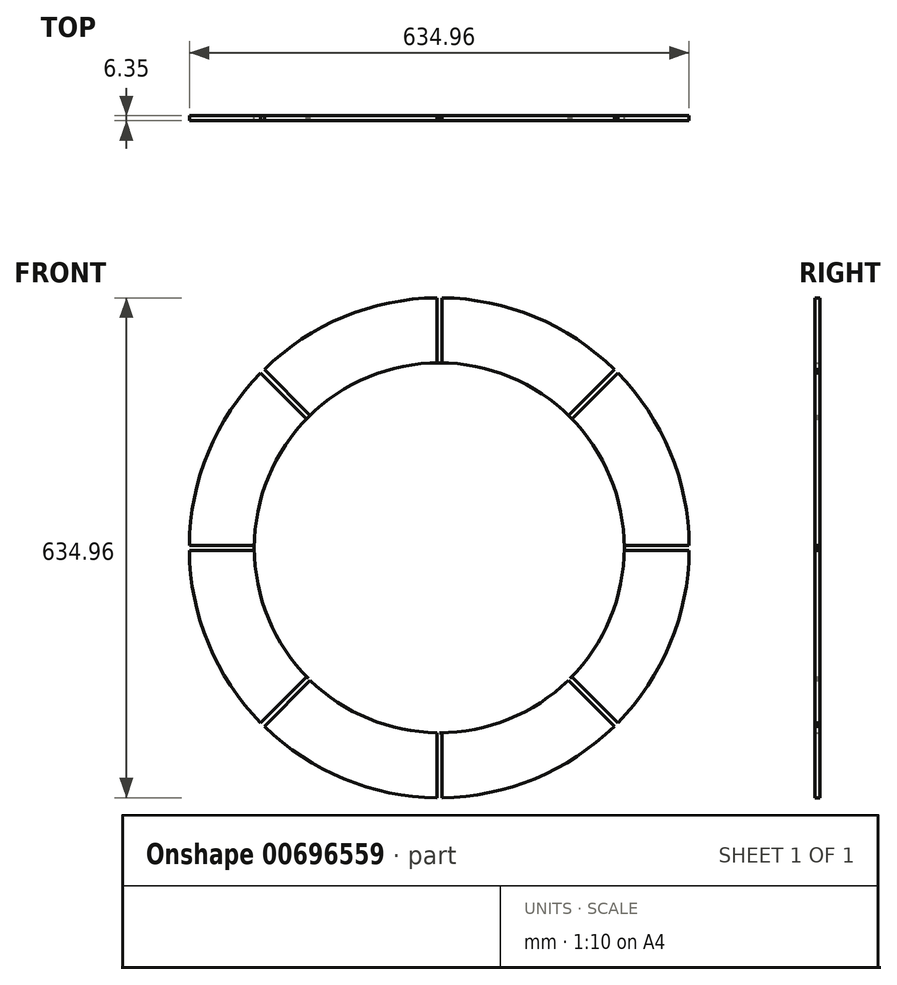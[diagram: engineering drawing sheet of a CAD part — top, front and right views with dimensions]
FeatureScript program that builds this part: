
annotation { "Feature Type Name" : "Feature", "Feature Type Description" : "" }
export const myFeature = defineFeature(function(context is Context, id is Id, definition is map)
    precondition{}
    {
        {
            var Q0;
            Q0=qCreatedBy(makeId("Front.planeOp"),FACE);
            var sketch = newSketch(context, id + "F0", { "sketchPlane" : qUnion([Q0])});
            skCircle(sketch, "E0", {"center": v(0, 0) * mm, "radius": 234.95 * mm});
            skCircle(sketch, "E1", {"center": v(0, 0) * mm, "radius": 317.5 * mm});
            skLineSegment(sketch, "E2", {"start": v(317.48, 0) * mm, "end": v(317.5, 0) * mm});
            skLineSegment(sketch, "E3", {"start": v(317.5, 0) * mm, "end": v(317.48, 0) * mm});
            skLineSegment(sketch, "E4", {"start": v(-317.48, 0) * mm, "end": v(-317.5, 0) * mm});
            skLineSegment(sketch, "E5", {"start": v(0, 317.5) * mm, "end": v(0, 317.5) * mm});
            skLineSegment(sketch, "E6", {"start": v(0, -317.48) * mm, "end": v(0, -317.5) * mm});
            skLineSegment(sketch, "E7.bottom", {"start": v(-317.5, 0) * mm, "end": v(-317.48, 0) * mm});
            skLineSegment(sketch, "E8", {"start": v(-224.5, 224.5) * mm, "end": v(-224.5, 224.5) * mm});
            skLineSegment(sketch, "E9", {"start": v(224.5, 224.5) * mm, "end": v(224.5, 224.5) * mm});
            skLineSegment(sketch, "E10", {"start": v(-224.5, -224.5) * mm, "end": v(-224.5, -224.5) * mm});
            skLineSegment(sketch, "E11", {"start": v(224.5, -224.5) * mm, "end": v(224.5, -224.5) * mm});
            skLineSegment(sketch, "E12", {"start": v(-166.13, -166.13) * mm, "end": v(-163.87, -168.36) * mm});
            skLineSegment(sketch, "E13", {"start": v(-166.13, -166.13) * mm, "end": v(-168.38, -163.89) * mm});
            skLineSegment(sketch, "E14", {"start": v(-168.38, -163.89) * mm, "end": v(-226.74, -222.25) * mm});
            skLineSegment(sketch, "E15", {"start": v(-163.87, -168.36) * mm, "end": v(-221.85, -227.13) * mm});
            skLineSegment(sketch, "E16", {"start": v(-221.85, -227.13) * mm, "end": v(-226.74, -222.25) * mm});
            skLineSegment(sketch, "E17", {"start": v(0, -234.95) * mm, "end": v(-3.17, -234.93) * mm});
            skLineSegment(sketch, "E18", {"start": v(0, -234.95) * mm, "end": v(3.18, -234.95) * mm});
            skLineSegment(sketch, "E19", {"start": v(-3.17, -234.93) * mm, "end": v(-3.17, -317.48) * mm});
            skLineSegment(sketch, "E20", {"start": v(3.18, -234.95) * mm, "end": v(3.18, -317.48) * mm});
            skLineSegment(sketch, "E21", {"start": v(3.18, -317.48) * mm, "end": v(-3.17, -317.48) * mm});
            skLineSegment(sketch, "E22", {"start": v(166.13, -166.13) * mm, "end": v(163.74, -168.22) * mm});
            skLineSegment(sketch, "E23", {"start": v(166.13, -166.13) * mm, "end": v(168.38, -163.89) * mm});
            skLineSegment(sketch, "E24", {"start": v(163.74, -168.22) * mm, "end": v(222.26, -226.73) * mm});
            skLineSegment(sketch, "E25", {"start": v(168.38, -163.89) * mm, "end": v(226.74, -222.25) * mm});
            skLineSegment(sketch, "E26", {"start": v(226.74, -222.25) * mm, "end": v(222.26, -226.73) * mm});
            skLineSegment(sketch, "E27", {"start": v(234.95, 0) * mm, "end": v(234.95, -3.17) * mm});
            skLineSegment(sketch, "E28", {"start": v(234.95, 0) * mm, "end": v(234.95, 3.18) * mm});
            skLineSegment(sketch, "E29", {"start": v(234.95, 3.18) * mm, "end": v(317.48, 3.18) * mm});
            skLineSegment(sketch, "E30", {"start": v(317.48, 3.18) * mm, "end": v(317.48, -3.18) * mm});
            skLineSegment(sketch, "E31", {"start": v(317.48, -3.18) * mm, "end": v(234.95, -3.17) * mm});
            skLineSegment(sketch, "E32", {"start": v(166.13, 166.13) * mm, "end": v(168.38, 163.89) * mm});
            skLineSegment(sketch, "E33", {"start": v(166.13, 166.13) * mm, "end": v(163.89, 168.38) * mm});
            skLineSegment(sketch, "E34", {"start": v(168.38, 163.89) * mm, "end": v(226.74, 222.25) * mm});
            skLineSegment(sketch, "E35", {"start": v(226.74, 222.25) * mm, "end": v(222.25, 226.74) * mm});
            skLineSegment(sketch, "E36", {"start": v(222.25, 226.74) * mm, "end": v(163.89, 168.38) * mm});
            skLineSegment(sketch, "E37", {"start": v(0, 234.95) * mm, "end": v(3.17, 234.95) * mm});
            skLineSegment(sketch, "E38", {"start": v(0, 234.95) * mm, "end": v(-3.17, 234.95) * mm});
            skLineSegment(sketch, "E39", {"start": v(-3.17, 234.95) * mm, "end": v(-3.17, 317.48) * mm});
            skLineSegment(sketch, "E40", {"start": v(-3.17, 317.48) * mm, "end": v(3.17, 317.5) * mm});
            skLineSegment(sketch, "E41", {"start": v(3.17, 317.5) * mm, "end": v(3.17, 234.95) * mm});
            skLineSegment(sketch, "E42", {"start": v(-166.13, 166.13) * mm, "end": v(-168.38, 163.89) * mm});
            skLineSegment(sketch, "E43", {"start": v(-166.13, 166.13) * mm, "end": v(-163.89, 168.38) * mm});
            skLineSegment(sketch, "E44", {"start": v(-168.38, 163.89) * mm, "end": v(-226.74, 222.25) * mm});
            skLineSegment(sketch, "E45", {"start": v(-226.74, 222.25) * mm, "end": v(-222.25, 226.74) * mm});
            skLineSegment(sketch, "E46", {"start": v(-222.25, 226.74) * mm, "end": v(-163.89, 168.38) * mm});
            skLineSegment(sketch, "E47", {"start": v(-234.95, 0) * mm, "end": v(-234.95, -3.18) * mm});
            skLineSegment(sketch, "E48", {"start": v(-234.95, 0) * mm, "end": v(-234.95, 3.17) * mm});
            skLineSegment(sketch, "E49", {"start": v(-234.95, 3.17) * mm, "end": v(-317.48, 3.17) * mm});
            skLineSegment(sketch, "E50", {"start": v(-317.48, 3.17) * mm, "end": v(-317.48, -3.18) * mm});
            skLineSegment(sketch, "E51", {"start": v(-317.48, -3.17) * mm, "end": v(-234.95, -3.18) * mm});
            skSolve(sketch);
        }
        {
            var Q0;
            Q0=makeQuery(id+"F0.imprint","IMPRINT",FACE,{"disambiguationData":[TD([[makeQuery(id+"F0.imprint","IMPRINT",EDGE,{"derivedFrom":sQuery(id+"F0.wireOp",EDGE,"E0")}),-1.0]])]});
            var Q1;
            {var subQ1=sQuery(id+"F0.wireOp",EDGE,"E13");Q1=makeQuery(id+"F0.imprint","IMPRINT",FACE,{"disambiguationData":[TD([[makeQuery(id+"F0.imprint","IMPRINT",EDGE,{"derivedFrom":subQ1}),-1.0]])]});}
            var Q2;
            {var subQ3=sQuery(id+"F0.wireOp",EDGE,"E42");Q2=makeQuery(id+"F0.imprint","IMPRINT",FACE,{"disambiguationData":[TD([[makeQuery(id+"F0.imprint","IMPRINT",EDGE,{"derivedFrom":subQ3}),1.0]])]});}
            var Q3;
            {var subQ0=sQuery(id+"F0.wireOp",EDGE,"E38");Q3=makeQuery(id+"F0.imprint","IMPRINT",FACE,{"disambiguationData":[TD([[makeQuery(id+"F0.imprint","IMPRINT",EDGE,{"derivedFrom":subQ0}),1.0]])]});}
            var Q4;
            {var subQ1=sQuery(id+"F0.wireOp",EDGE,"E33");Q4=makeQuery(id+"F0.imprint","IMPRINT",FACE,{"disambiguationData":[TD([[makeQuery(id+"F0.imprint","IMPRINT",EDGE,{"derivedFrom":subQ1}),1.0]])]});}
            var Q5;
            {var subQ0=sQuery(id+"F0.wireOp",EDGE,"E28");Q5=makeQuery(id+"F0.imprint","IMPRINT",FACE,{"disambiguationData":[TD([[makeQuery(id+"F0.imprint","IMPRINT",EDGE,{"derivedFrom":subQ0}),1.0]])]});}
            var Q6;
            {var subQ0=sQuery(id+"F0.wireOp",EDGE,"E23");Q6=makeQuery(id+"F0.imprint","IMPRINT",FACE,{"disambiguationData":[TD([[makeQuery(id+"F0.imprint","IMPRINT",EDGE,{"derivedFrom":subQ0}),1.0]])]});}
            var Q7;
            {var subQ0=sQuery(id+"F0.wireOp",EDGE,"E18");Q7=makeQuery(id+"F0.imprint","IMPRINT",FACE,{"disambiguationData":[TD([[makeQuery(id+"F0.imprint","IMPRINT",EDGE,{"derivedFrom":subQ0}),1.0]])]});}
            extrude(context, id + "F1", {"entities" : qUnion([Q0, Q1, Q2, Q3, Q4, Q5, Q6, Q7]), "depth" : 6.35 * mm, "offsetDistance" : 25.4 * mm});
        }
    });
